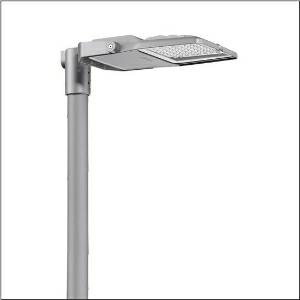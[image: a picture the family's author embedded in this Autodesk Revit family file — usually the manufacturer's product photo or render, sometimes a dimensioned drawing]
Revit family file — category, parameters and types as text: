
# Revit family: floodlight_fl_21_mini___pl52_5xa7775d2d3a_ca02
name_source: partatom
category: Lighting Fixtures
units: mm (PartAtom-declared; Revit-internal decimal feet)

## family parameters
Cut with Voids When Loaded = No
Host = Face
Light Source = No
Part Type = Normal
Room Calculation Point = No
Round Connector Dimension = Use Diameter
Shared = No

## types (1)
- --- (1 x LED, 17840 lm, 142.9 W, 3000K)
    Apparent Load = 143 VA
    CIE Flux Codes = 26 60 98 100 100
    Color Rendering = 70
    Color Temperature = 3000K
    Default Elevation = 1800 mm
    Description = Floodlight FL 21 mini, floodlight, primary light control with lens, of PMMA, primary optical cover: protective disc, of toughened safety glass, transparent, light distribution: PL52, light emission: direct distribution, installation type: surface-mounted, LED, High Power LED, rated luminous flux: 17.840lm, luminous efficacy: 125lm/W, light colour: 730, colour temperature: 3000K, control gear: ECG Smart Interface, control: flexible luminous flux parameterisation, time-dependent luminous flux control, constant luminous flux control, overheat protection, presetting dimming logarithmic, with terminal, 6-pole, mains connection: 220..240V, AC, 50/60Hz, start of lifetime: 143W, end of lifetime: 151W, reduction: 63W, luminaire housing, of diecast aluminium, powder-coated, Siteco® metallic grey (DB 702S), corrosivity category C5 according to DIN EN ISO 12944, mast bracket, of steel, galvanised, powder-coated, Siteco® metallic grey (DB 702S), protection rating (complete): IP66, insulation class (complete): insulation class II (safety insulation), certification: CE, ENEC, VDE, protection symbol: D, impact resistance: IK08, permissible operating ambient temperature: -40..+40°C, permissible operating ambient temperature for outdoor applications: -40..+50°C, standard: DIN EN 12944, packaging unit: 1 piece

Light Distribution: PL52
    Height = 70 mm
    Lamp = 1 x LED
    Lamp Light Flux = 17840 lm
    Lamp Power = 142.9 W
    Lamp count = 1
    Length = 485 mm
    Luminous efficacy = 125 lm/W
    Manufacturer = Siteco
    ModVariant = No
    Model = 5XA7775D2D3A
    Number of Poles = 1
    OnlyDefault = Yes
    Power Factor = 1
    Product Name = Floodlight FL 21 mini | PL52
    Product group = floodlight | pylon top
    ProductGroupID = 6101
    Protection Class = Protection class II
    Protection Degree = IP 66
    RLX_Detail_Level = 1
    RlxData = <blob elided: 101373 chars, md5=f6970897>
    Socket = socket
    Standby Power = 0 W
    System Light Flux = 17840 lm
    System Power = 143 W
    Type Comments = factory setting: luminous flux: 100 % | dim-lin: 254 | 730 mA
    Type Image = l_1007125.jpg
    URL = http://relux.com
    VarID = @adj_074373
    Voltage = 0 V
    Weight = 0.00 kg
    Width = 337 mm

## geometry (parser evidence)
native form markers: Blend x4, Sweep x12
no freeform markers — native parametric forms only
